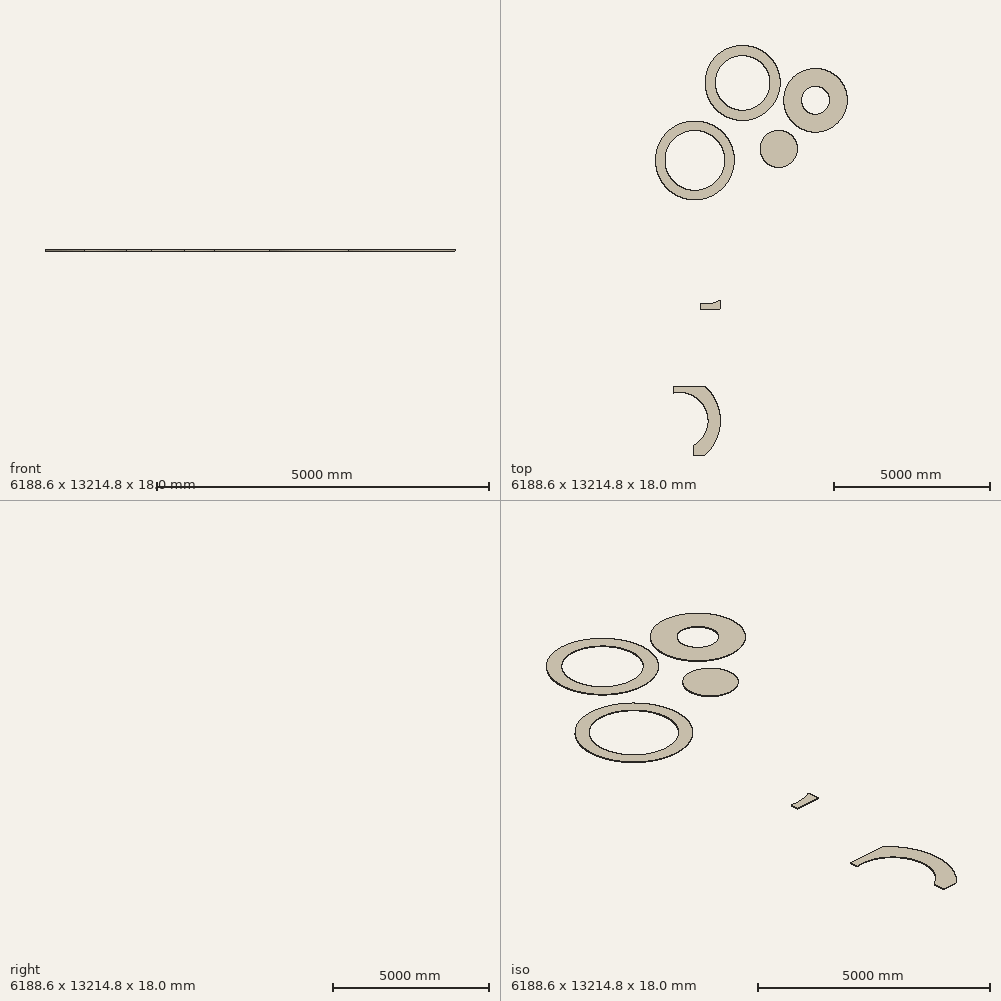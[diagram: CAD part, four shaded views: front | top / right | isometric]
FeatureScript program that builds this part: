
annotation { "Feature Type Name" : "Feature", "Feature Type Description" : "" }
export const myFeature = defineFeature(function(context is Context, id is Id, definition is map)
    precondition{}
    {
        {
            var Q0;
            Q0=qCreatedBy(makeId("Top.planeOp"),FACE);
            var sketch = newSketch(context, id + "F0", { "sketchPlane" : qUnion([Q0])});
            skCircle(sketch, "E0", {"center": v(0, 0) * mm, "radius": 600 * mm});
            skSolve(sketch);
        }
        {
            var Q0;
            Q0=makeQuery(id+"F0.imprint","IMPRINT",FACE,{"disambiguationData":[TD([[makeQuery(id+"F0.imprint","IMPRINT",EDGE,{"derivedFrom":sQuery(id+"F0.wireOp",EDGE,"E0")}),1.0]])]});
            extrude(context, id + "F1", {"entities" : qUnion([Q0]), "depth" : 18 * mm, "offsetDistance" : 25 * mm});
        }
        {
            var Q0;
            Q0=qCreatedBy(makeId("Top.planeOp"),FACE);
            var sketch = newSketch(context, id + "F2", { "sketchPlane" : qUnion([Q0])});
            skCircle(sketch, "E1", {"center": v(1183.2, 1567.85) * mm, "radius": 1027 * mm});
            skCircle(sketch, "E2", {"center": v(1183.2, 1567.85) * mm, "radius": 450 * mm});
            skSolve(sketch);
        }
        {
            var Q0;
            Q0=makeQuery(id+"F2.imprint","IMPRINT",FACE,{"disambiguationData":[TD([[makeQuery(id+"F2.imprint","IMPRINT",EDGE,{"derivedFrom":sQuery(id+"F2.wireOp",EDGE,"E1")}),1.0]])]});
            extrude(context, id + "F3", {"entities" : qUnion([Q0]), "depth" : 18 * mm, "offsetDistance" : 25 * mm});
        }
        {
            var Q0;
            Q0=qCreatedBy(makeId("Top.planeOp"),FACE);
            var sketch = newSketch(context, id + "F4", { "sketchPlane" : qUnion([Q0])});
            skCircle(sketch, "E3", {"center": v(-1167.27, 2126.68) * mm, "radius": 1210 * mm});
            skCircle(sketch, "E4", {"center": v(-1167.27, 2126.68) * mm, "radius": 880 * mm});
            skSolve(sketch);
        }
        {
            var Q0;
            Q0=makeQuery(id+"F4.imprint","IMPRINT",FACE,{"disambiguationData":[TD([[makeQuery(id+"F4.imprint","IMPRINT",EDGE,{"derivedFrom":sQuery(id+"F4.wireOp",EDGE,"E3")}),1.0]])]});
            extrude(context, id + "F5", {"entities" : qUnion([Q0]), "depth" : 18 * mm, "offsetDistance" : 25 * mm});
        }
        {
            var Q0;
            Q0=qCreatedBy(makeId("Top.planeOp"),FACE);
            var sketch = newSketch(context, id + "F6", { "sketchPlane" : qUnion([Q0])});
            skCircle(sketch, "E5", {"center": v(-2705.94, -369.3) * mm, "radius": 1272.5 * mm});
            skCircle(sketch, "E6", {"center": v(-2705.94, -369.3) * mm, "radius": 965 * mm});
            skSolve(sketch);
        }
        {
            var Q0;
            Q0=makeQuery(id+"F6.imprint","IMPRINT",FACE,{"disambiguationData":[TD([[makeQuery(id+"F6.imprint","IMPRINT",EDGE,{"derivedFrom":sQuery(id+"F6.wireOp",EDGE,"E5")}),1.0]])]});
            extrude(context, id + "F7", {"entities" : qUnion([Q0]), "depth" : 18 * mm, "offsetDistance" : 25 * mm});
        }
        {
            var Q0;
            Q0=qCreatedBy(makeId("Top.planeOp"),FACE);
            var sketch = newSketch(context, id + "F8", { "sketchPlane" : qUnion([Q0])});
            skLineSegment(sketch, "E7", {"start": v(-2527.64, -6162.49) * mm, "end": v(-2527.64, -5575.06) * mm, "construction": true});
            skLineSegment(sketch, "E8", {"start": v(-5668.34, -4075.06) * mm, "end": v(976.06, -4075.06) * mm, "construction": true});
            skLineSegment(sketch, "E9", {"start": v(-5640.44, -2963.06) * mm, "end": v(-2039.87, -2963.06) * mm, "construction": true});
            skLineSegment(sketch, "E10.MirrorCS", {"start": v(-5640.44, -5187.06) * mm, "end": v(-2039.87, -5187.06) * mm, "construction": true});
            skPoint(sketch, "E11", {"position": v(-2346.14, -4075.06) * mm});
            skArc(sketch, "E12", {"start": v(-3662.17, -4075.06) * mm, "mid": v(-3499, -4709.75) * mm, "end": v(-3049.98, -5187.06) * mm});
            skLineSegment(sketch, "E13", {"start": v(-2527.64, -4976.98) * mm, "end": v(-2527.64, -5378.52) * mm});
            skLineSegment(sketch, "E14", {"start": v(-2527.64, -2575.06) * mm, "end": v(-2527.64, -3173.14) * mm});
            skLineSegment(sketch, "E15", {"start": v(-2527.64, -4976.98) * mm, "end": v(-2527.64, -2963.06) * mm, "construction": true});
            skArc(sketch, "E16", {"start": v(-2527.64, -4976.98) * mm, "mid": v(-1426.14, -4075.06) * mm, "end": v(-2527.64, -3173.14) * mm});
            skLineSegment(sketch, "E17", {"start": v(-2527.64, -5187.06) * mm, "end": v(-2527.64, -4976.98) * mm, "construction": true});
            skArc(sketch, "E18", {"start": v(-2527.64, -2575.06) * mm, "mid": v(-3927.28, -3535.62) * mm, "end": v(-3534.34, -5187.06) * mm});
            skArc(sketch, "E19", {"start": v(-2527.64, -5575.06) * mm, "mid": v(-2525.7, -5575.06) * mm, "end": v(-2523.75, -5575.06) * mm});
            skArc(sketch, "E20", {"start": v(-1520.93, -5187.06) * mm, "mid": v(-1027.64, -4070.87) * mm, "end": v(-1527.16, -2957.45) * mm});
            skArc(sketch, "E21.trimOffspring", {"start": v(-1642.29, -5187.06) * mm, "mid": v(-1193.26, -4709.75) * mm, "end": v(-1030.1, -4075.06) * mm});
            skLineSegment(sketch, "E22", {"start": v(-2527.64, -5378.52) * mm, "end": v(-2523.75, -5575.06) * mm});
            skLineSegment(sketch, "E23", {"start": v(-2527.64, -2963.06) * mm, "end": v(-1527.16, -2957.45) * mm});
            skLineSegment(sketch, "E24", {"start": v(-2527.64, -5187.06) * mm, "end": v(-1642.29, -5187.06) * mm});
            skLineSegment(sketch, "E25", {"start": v(-1642.29, -5187.06) * mm, "end": v(-1520.93, -5187.06) * mm});
            skLineSegment(sketch, "E26", {"start": v(-2346.14, -2595.6) * mm, "end": v(-2346.14, -5611.52) * mm, "construction": true});
            skLineSegment(sketch, "E27", {"start": v(-1896.14, -4768.69) * mm, "end": v(-1896.14, -5406.56) * mm, "construction": true});
            skLineSegment(sketch, "E28", {"start": v(-1896.14, -4877.5) * mm, "end": v(-1896.14, -5187.06) * mm});
            skSolve(sketch);
        }
        {
            var Q0;
            {var subQ0=sQuery(id+"F8.wireOp",EDGE,"E16");Q0=makeQuery(id+"F8.imprint","IMPRINT",FACE,{"disambiguationData":[TD([[makeQuery(id+"F8.imprint","IMPRINT",EDGE,{"derivedFrom":subQ0}),-1.0]])]});}
            extrude(context, id + "F9", {"entities" : qUnion([Q0]), "depth" : 18 * mm, "offsetDistance" : 25 * mm});
        }
        {
            var Q0;
            Q0=makeQuery(id+"F8.imprint","IMPRINT",FACE,{"disambiguationData":[TD([[makeQuery(id+"F8.imprint","IMPRINT",EDGE,{"derivedFrom":sQuery(id+"F8.wireOp",EDGE,"E20")}),1.0]])]});
            var sketch = newSketch(context, id + "F10", { "sketchPlane" : qUnion([Q0])});
            skLineSegment(sketch, "E29", {"start": v(-3383.76, -10853.57) * mm, "end": v(-3383.76, -10266.15) * mm, "construction": true});
            skLineSegment(sketch, "E30", {"start": v(-6524.46, -8766.15) * mm, "end": v(119.94, -8766.15) * mm, "construction": true});
            skLineSegment(sketch, "E31", {"start": v(-6496.57, -7654.15) * mm, "end": v(-2896, -7654.15) * mm, "construction": true});
            skLineSegment(sketch, "E32.MirrorCS", {"start": v(-6496.57, -9878.15) * mm, "end": v(-2896, -9878.15) * mm, "construction": true});
            skPoint(sketch, "E33", {"position": v(-3202.26, -8766.15) * mm});
            skArc(sketch, "E34", {"start": v(-4518.3, -8766.15) * mm, "mid": v(-4355.14, -9400.83) * mm, "end": v(-3906.1, -9878.15) * mm});
            skLineSegment(sketch, "E35", {"start": v(-3383.76, -9668.06) * mm, "end": v(-3383.76, -10069.6) * mm});
            skLineSegment(sketch, "E36", {"start": v(-3383.76, -7266.15) * mm, "end": v(-3383.76, -7864.23) * mm});
            skLineSegment(sketch, "E37", {"start": v(-3383.76, -9668.06) * mm, "end": v(-3383.76, -7654.15) * mm, "construction": true});
            skArc(sketch, "E38", {"start": v(-3383.76, -9668.06) * mm, "mid": v(-2282.26, -8766.15) * mm, "end": v(-3383.76, -7864.23) * mm});
            skLineSegment(sketch, "E39", {"start": v(-3383.76, -9878.15) * mm, "end": v(-3383.76, -9668.06) * mm, "construction": true});
            skArc(sketch, "E40", {"start": v(-3383.76, -7266.15) * mm, "mid": v(-4783.4, -8226.7) * mm, "end": v(-4390.47, -9878.15) * mm});
            skArc(sketch, "E41", {"start": v(-3383.76, -10266.15) * mm, "mid": v(-3381.82, -10266.14) * mm, "end": v(-3379.88, -10266.14) * mm});
            skArc(sketch, "E42", {"start": v(-2377.06, -9878.15) * mm, "mid": v(-1883.77, -8761.95) * mm, "end": v(-2383.29, -7648.53) * mm});
            skArc(sketch, "E43.trimOffspring", {"start": v(-2498.41, -9878.15) * mm, "mid": v(-2049.39, -9400.83) * mm, "end": v(-1886.23, -8766.15) * mm});
            skLineSegment(sketch, "E44", {"start": v(-3383.76, -10069.6) * mm, "end": v(-3379.88, -10266.14) * mm});
            skLineSegment(sketch, "E45", {"start": v(-3383.76, -7654.15) * mm, "end": v(-2383.29, -7648.53) * mm});
            skLineSegment(sketch, "E46", {"start": v(-3383.76, -9878.15) * mm, "end": v(-2498.41, -9878.15) * mm});
            skLineSegment(sketch, "E47", {"start": v(-2498.41, -9878.15) * mm, "end": v(-2377.06, -9878.15) * mm});
            skLineSegment(sketch, "E48", {"start": v(-3202.26, -7286.68) * mm, "end": v(-3202.26, -10302.6) * mm, "construction": true});
            skLineSegment(sketch, "E49", {"start": v(-2752.26, -9459.77) * mm, "end": v(-2752.26, -10097.65) * mm, "construction": true});
            skLineSegment(sketch, "E50", {"start": v(-2752.26, -9568.58) * mm, "end": v(-2752.26, -9878.15) * mm});
            skSolve(sketch);
        }
        {
            var Q0;
            Q0=makeQuery(id+"F10.imprint","IMPRINT",FACE,{"disambiguationData":[TD([[makeQuery(id+"F10.imprint","IMPRINT",EDGE,{"derivedFrom":sQuery(id+"F10.wireOp",EDGE,"E42")}),1.0]])]});
            extrude(context, id + "F11", {"entities" : qUnion([Q0]), "depth" : 18 * mm, "offsetDistance" : 25 * mm});
        }
    });
